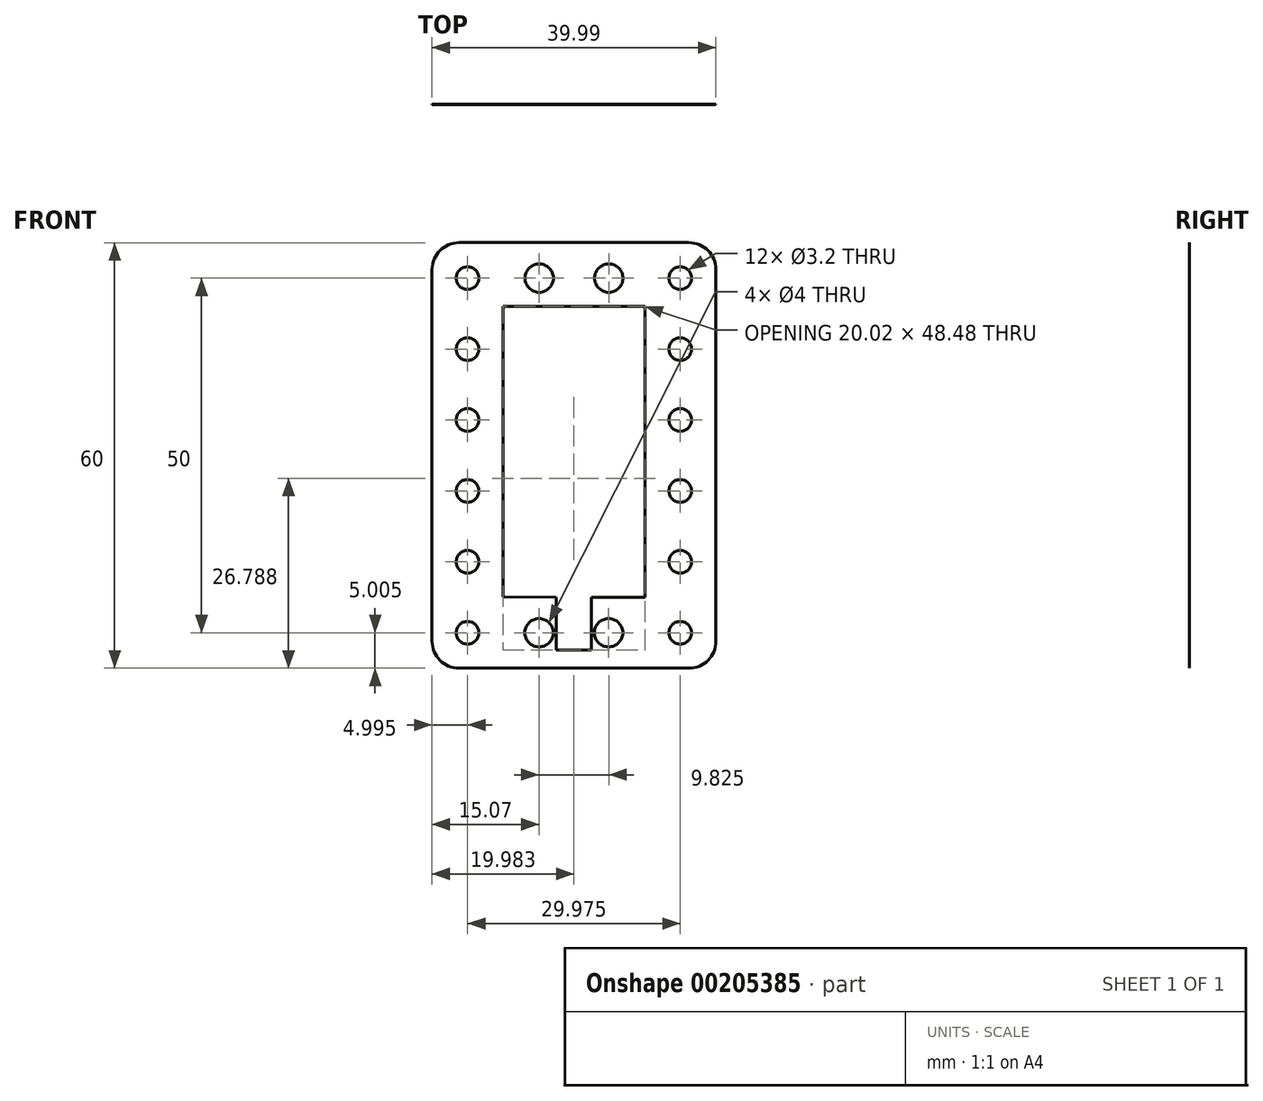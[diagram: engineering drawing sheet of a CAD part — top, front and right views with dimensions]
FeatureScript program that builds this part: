
annotation { "Feature Type Name" : "Feature", "Feature Type Description" : "" }
export const myFeature = defineFeature(function(context is Context, id is Id, definition is map)
    precondition{}
    {
        {
            var Q0;
            Q0=qCreatedBy(makeId("Front.planeOp"),FACE);
            var sketch = newSketch(context, id + "F0", { "sketchPlane" : qUnion([Q0])});
            skLineSegment(sketch, "E0.left", {"start": v(0, 0) * mm, "end": v(0, -41) * mm});
            skLineSegment(sketch, "E1.bottom", {"start": v(-6.16, 8.97) * mm, "end": v(26.22, 8.97) * mm});
            skLineSegment(sketch, "E1.top", {"start": v(-6.16, -51.03) * mm, "end": v(26.22, -51.03) * mm});
            skLineSegment(sketch, "E1.left", {"start": v(-9.97, 5.16) * mm, "end": v(-9.97, -47.22) * mm});
            skLineSegment(sketch, "E1.right", {"start": v(30.03, 5.16) * mm, "end": v(30.03, -47.22) * mm});
            skCircle(sketch, "E2", {"center": v(-4.97, 3.97) * mm, "radius": 1.6 * mm});
            skCircle(sketch, "E3.3.0.0", {"center": v(25, 3.97) * mm, "radius": 1.6 * mm});
            skLineSegment(sketch, "E3.direction1", {"start": v(-4.97, 3.97) * mm, "end": v(5.03, 3.97) * mm, "construction": true});
            skCircle(sketch, "E4.0.1.0", {"center": v(-4.97, -6.03) * mm, "radius": 1.6 * mm});
            skCircle(sketch, "E4.0.2.0", {"center": v(-4.97, -16.03) * mm, "radius": 1.6 * mm});
            skCircle(sketch, "E4.0.3.0", {"center": v(-4.97, -26.03) * mm, "radius": 1.6 * mm});
            skCircle(sketch, "E4.0.4.0", {"center": v(-4.97, -36.03) * mm, "radius": 1.6 * mm});
            skCircle(sketch, "E4.0.5.0", {"center": v(-4.97, -46.03) * mm, "radius": 1.6 * mm});
            skLineSegment(sketch, "E4.direction1", {"start": v(-4.97, 3.97) * mm, "end": v(20.38, 3.97) * mm, "construction": true});
            skLineSegment(sketch, "E4.direction2", {"start": v(-4.97, 3.97) * mm, "end": v(-4.97, -6.03) * mm, "construction": true});
            skCircle(sketch, "E5.0.1.0", {"center": v(25, -6.03) * mm, "radius": 1.6 * mm});
            skCircle(sketch, "E5.0.2.0", {"center": v(25, -16.03) * mm, "radius": 1.6 * mm});
            skCircle(sketch, "E5.0.3.0", {"center": v(25, -26.03) * mm, "radius": 1.6 * mm});
            skCircle(sketch, "E5.0.4.0", {"center": v(25, -36.03) * mm, "radius": 1.6 * mm});
            skCircle(sketch, "E5.0.5.0", {"center": v(25, -46.03) * mm, "radius": 1.6 * mm});
            skLineSegment(sketch, "E5.direction1", {"start": v(25, 3.97) * mm, "end": v(50.38, 3.97) * mm, "construction": true});
            skLineSegment(sketch, "E5.direction2", {"start": v(25, 3.97) * mm, "end": v(25, -6.03) * mm, "construction": true});
            skLineSegment(sketch, "E6.direction1", {"start": v(-4.97, -46.03) * mm, "end": v(5.03, -46.03) * mm, "construction": true});
            skCircle(sketch, "E7", {"center": v(5.13, 3.97) * mm, "radius": 2 * mm});
            skCircle(sketch, "E8", {"center": v(14.93, 3.97) * mm, "radius": 2 * mm});
            skCircle(sketch, "E9.MirrorC", {"center": v(5.1, -46.03) * mm, "radius": 2 * mm});
            skCircle(sketch, "E10.MirrorC", {"center": v(14.9, -46.03) * mm, "radius": 2 * mm});
            skLineSegment(sketch, "E11.top", {"start": v(7.52, -48.49) * mm, "end": v(12.47, -48.49) * mm});
            skLineSegment(sketch, "E11.left", {"start": v(7.52, -41.03) * mm, "end": v(7.52, -48.49) * mm});
            skLineSegment(sketch, "E11.right", {"start": v(12.47, -41.03) * mm, "end": v(12.47, -48.49) * mm});
            skPoint(sketch, "E12.visualSharp", {"position": v(-9.97, 8.97) * mm});
            skArc(sketch, "E12.filletArc", {"start": v(-6.16, 8.97) * mm, "mid": v(-8.86, 7.86) * mm, "end": v(-9.97, 5.16) * mm});
            skPoint(sketch, "E13.visualSharp", {"position": v(-9.97, -51.03) * mm});
            skArc(sketch, "E13.filletArc", {"start": v(-9.98, -47.22) * mm, "mid": v(-8.86, -49.9) * mm, "end": v(-6.16, -51.03) * mm});
            skPoint(sketch, "E14.visualSharp", {"position": v(30.03, -51.03) * mm});
            skArc(sketch, "E14.filletArc", {"start": v(26.22, -51.03) * mm, "mid": v(28.9, -49.9) * mm, "end": v(30.03, -47.22) * mm});
            skPoint(sketch, "E15.visualSharp", {"position": v(30.03, 8.97) * mm});
            skArc(sketch, "E15.filletArc", {"start": v(30.03, 5.16) * mm, "mid": v(28.9, 7.86) * mm, "end": v(26.22, 8.97) * mm});
            skLineSegment(sketch, "E16", {"start": v(0, 0) * mm, "end": v(20.03, 0) * mm});
            skLineSegment(sketch, "E17", {"start": v(20.03, 0) * mm, "end": v(20.03, -41.03) * mm});
            skLineSegment(sketch, "E18", {"start": v(0, -41) * mm, "end": v(7.52, -41.03) * mm});
            skLineSegment(sketch, "E19", {"start": v(12.47, -41.03) * mm, "end": v(20.03, -41.03) * mm});
            skSolve(sketch);
        }
        {
            var Q0;
            Q0=makeQuery(id+"F0.imprint","IMPRINT",FACE,{"disambiguationData":[TD([[makeQuery(id+"F0.imprint","IMPRINT",EDGE,{"derivedFrom":sQuery(id+"F0.wireOp",EDGE,"E0.left")}),-1.0]])]});
            extrude(context, id + "F1", {"entities" : qUnion([Q0]), "depth" : 1 / 203.2 * mm});
        }
    });
